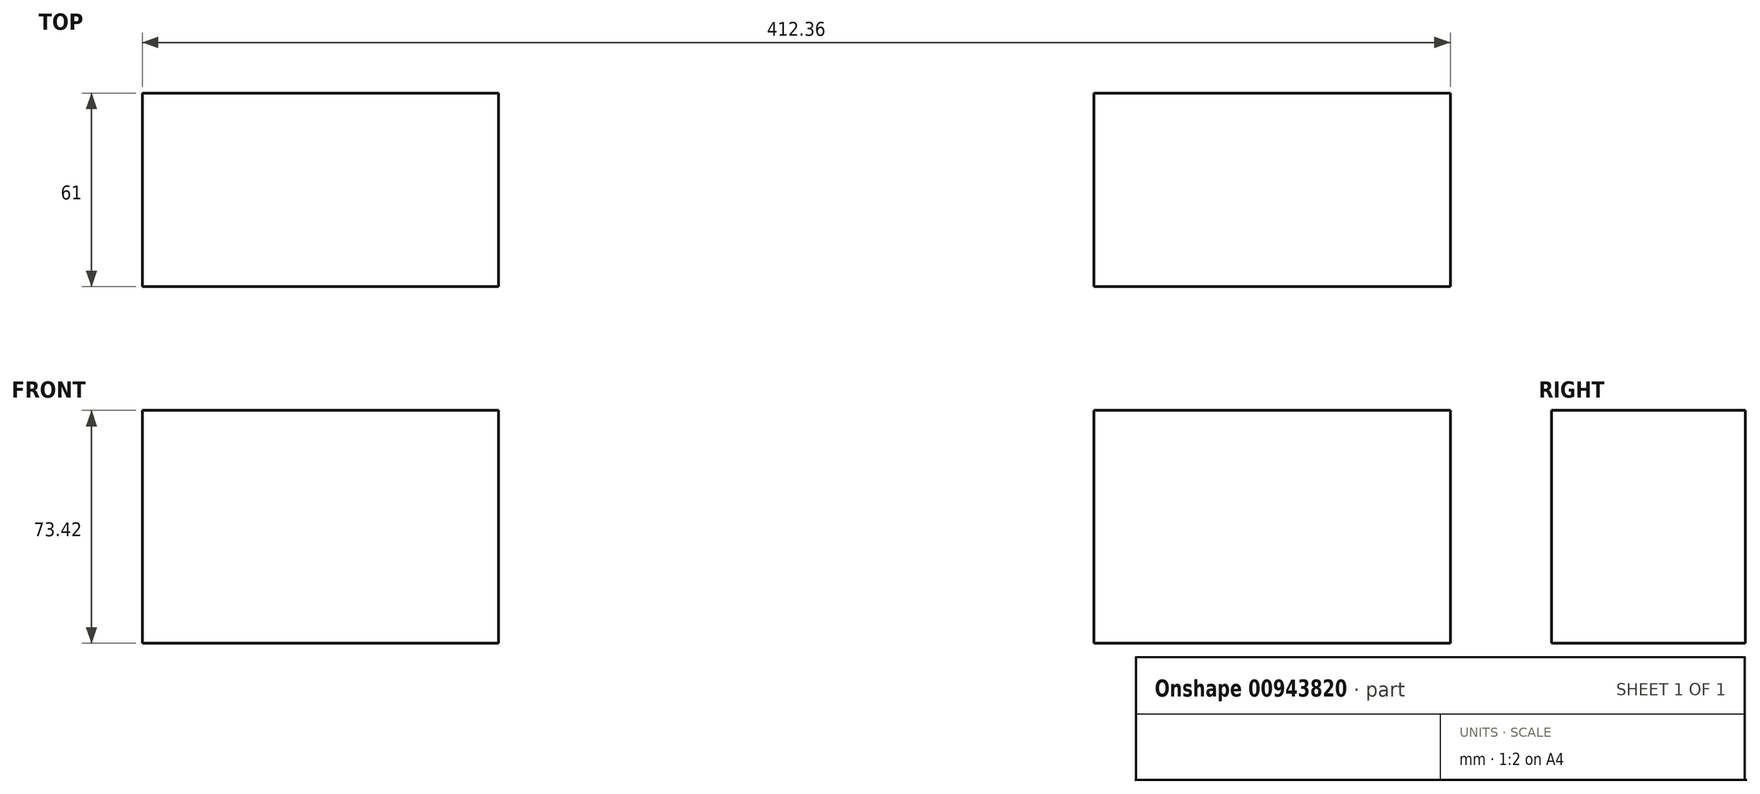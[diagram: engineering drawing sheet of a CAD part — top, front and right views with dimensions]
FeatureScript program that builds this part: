
annotation { "Feature Type Name" : "Feature", "Feature Type Description" : "" }
export const myFeature = defineFeature(function(context is Context, id is Id, definition is map)
    precondition{}
    {
        {
            var Q0;
            Q0=qCreatedBy(makeId("Front.planeOp"),FACE);
            var sketch = newSketch(context, id + "F0", { "sketchPlane" : qUnion([Q0])});
            skLineSegment(sketch, "E0.bottom", {"start": v(-206.18, 77.2) * mm, "end": v(-93.86, 77.2) * mm});
            skLineSegment(sketch, "E0.top", {"start": v(-206.18, 3.77) * mm, "end": v(-93.86, 3.77) * mm});
            skLineSegment(sketch, "E0.left", {"start": v(-206.18, 77.2) * mm, "end": v(-206.18, 3.77) * mm});
            skLineSegment(sketch, "E0.right", {"start": v(-93.86, 77.2) * mm, "end": v(-93.86, 3.77) * mm});
            skLineSegment(sketch, "E1.MirrorCS", {"start": v(206.18, 3.77) * mm, "end": v(93.86, 3.77) * mm});
            skLineSegment(sketch, "E2.MirrorCS", {"start": v(93.86, 77.2) * mm, "end": v(93.86, 3.77) * mm});
            skLineSegment(sketch, "E3.MirrorCS", {"start": v(206.18, 77.2) * mm, "end": v(206.18, 3.77) * mm});
            skLineSegment(sketch, "E4.MirrorCS", {"start": v(206.18, 77.2) * mm, "end": v(93.86, 77.2) * mm});
            skSolve(sketch);
        }
        {
            var Q0;
            Q0=makeQuery(id+"F0.imprint","IMPRINT",FACE,{"disambiguationData":[TD([[makeQuery(id+"F0.imprint","IMPRINT",EDGE,{"derivedFrom":sQuery(id+"F0.wireOp",EDGE,"E0.bottom")}),-1.0]])]});
            var Q1;
            Q1=makeQuery(id+"F0.imprint","IMPRINT",FACE,{"disambiguationData":[TD([[makeQuery(id+"F0.imprint","IMPRINT",EDGE,{"derivedFrom":sQuery(id+"F0.wireOp",EDGE,"E1.MirrorCS")}),-1.0]])]});
            extrude(context, id + "F1", {"entities" : qUnion([Q0, Q1]), "depth" : 61 * mm, "offsetDistance" : 25 * mm});
        }
    });
